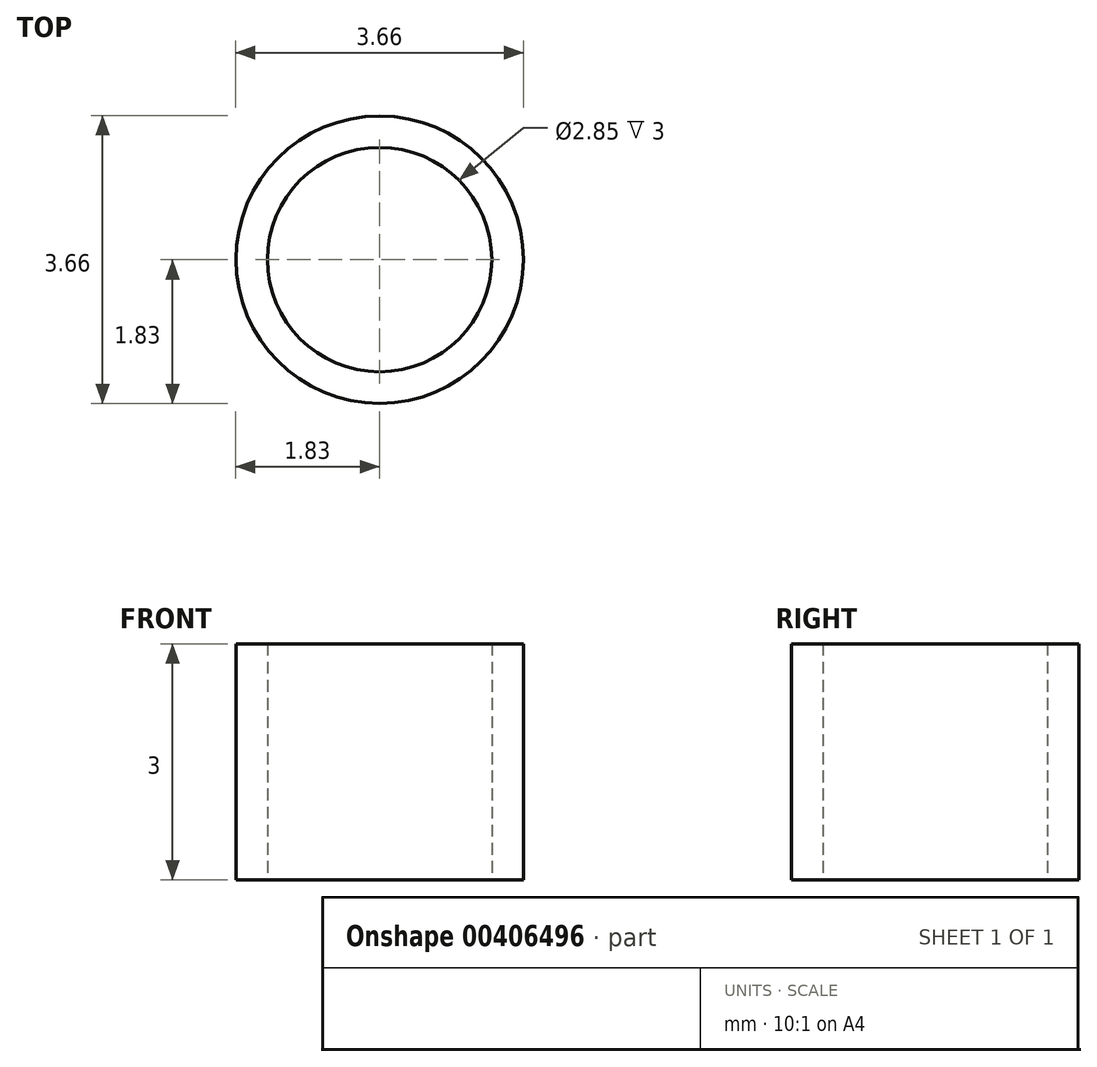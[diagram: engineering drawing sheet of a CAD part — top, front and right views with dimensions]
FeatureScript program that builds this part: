
annotation { "Feature Type Name" : "Feature", "Feature Type Description" : "" }
export const myFeature = defineFeature(function(context is Context, id is Id, definition is map)
    precondition{}
    {
        {
            var Q0;
            Q0=qCreatedBy(makeId("Top.planeOp"),FACE);
            var sketch = newSketch(context, id + "F0", { "sketchPlane" : qUnion([Q0])});
            skCircle(sketch, "E0", {"center": v(0, 0) * mm, "radius": 1.43 * mm});
            skCircle(sketch, "E1", {"center": v(0, 0) * mm, "radius": 1.82 * mm});
            skSolve(sketch);
        }
        {
            var Q0;
            Q0=makeQuery(id+"F0.imprint","IMPRINT",FACE,{"disambiguationData":[TD([[makeQuery(id+"F0.imprint","IMPRINT",EDGE,{"derivedFrom":sQuery(id+"F0.wireOp",EDGE,"E0")}),-1.0]])]});
            extrude(context, id + "F1", {"entities" : qUnion([Q0]), "depth" : 3 * mm});
        }
    });
